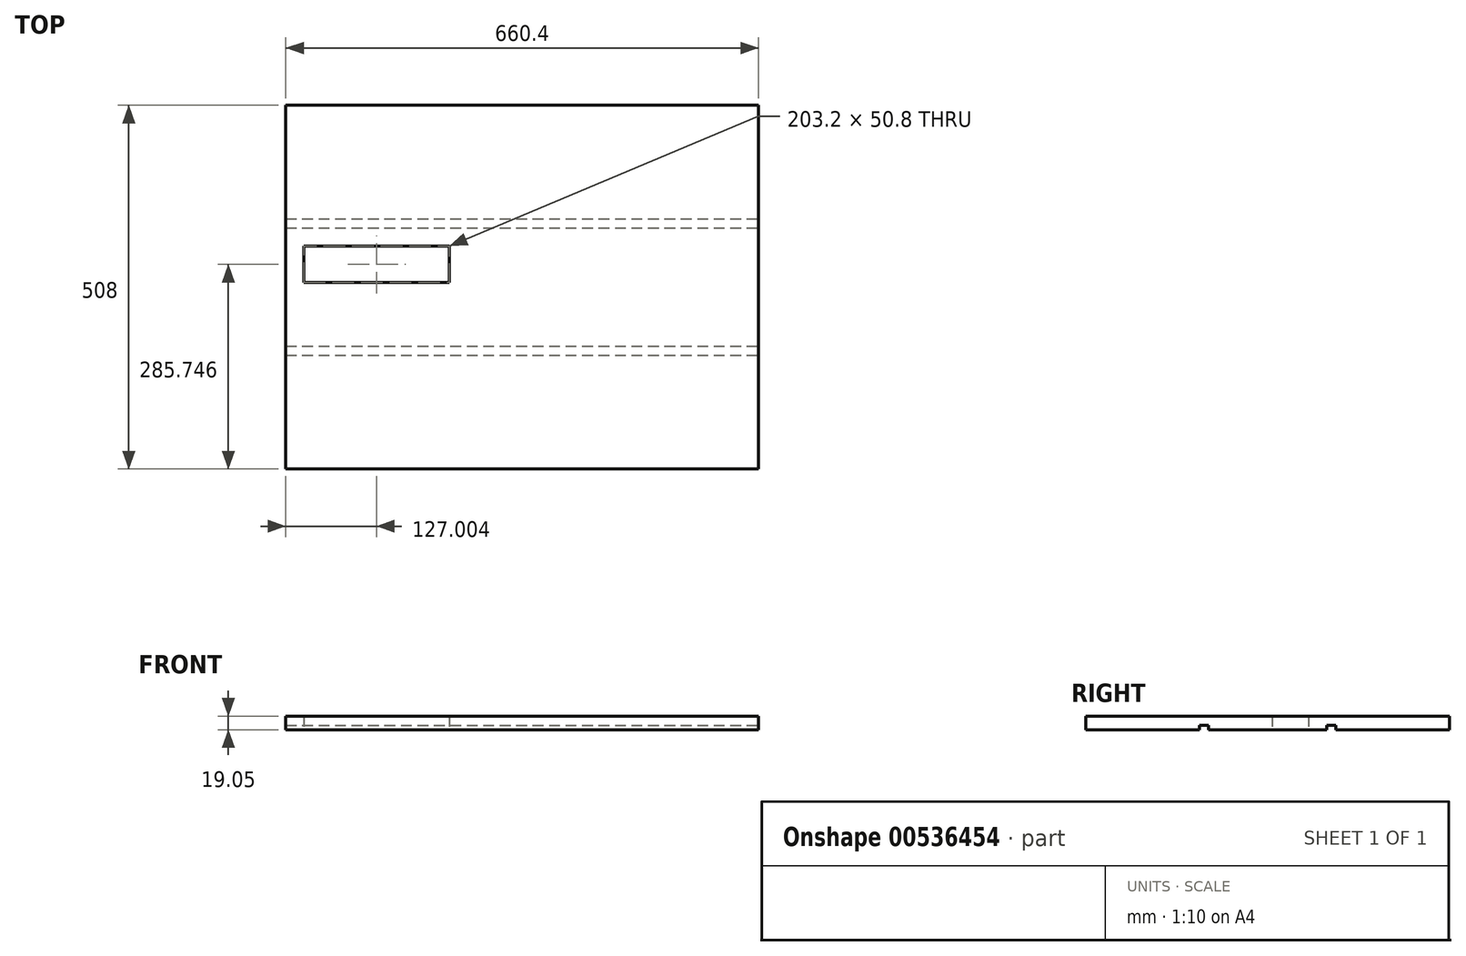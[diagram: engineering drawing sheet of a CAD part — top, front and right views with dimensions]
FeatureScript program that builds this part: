
annotation { "Feature Type Name" : "Feature", "Feature Type Description" : "" }
export const myFeature = defineFeature(function(context is Context, id is Id, definition is map)
    precondition{}
    {
        {
            var Q0;
            Q0=qCreatedBy(makeId("Top.planeOp"),FACE);
            var sketch = newSketch(context, id + "F0", { "sketchPlane" : qUnion([Q0])});
            skLineSegment(sketch, "E0.bottom", {"start": v(-46.34, 447.39) * mm, "end": v(614.06, 447.39) * mm});
            skLineSegment(sketch, "E0.top", {"start": v(-46.34, -60.61) * mm, "end": v(614.06, -60.61) * mm});
            skLineSegment(sketch, "E0.left", {"start": v(-46.34, 447.39) * mm, "end": v(-46.34, -60.61) * mm});
            skLineSegment(sketch, "E0.right", {"start": v(614.06, 447.39) * mm, "end": v(614.06, 415.64) * mm});
            skPoint(sketch, "E1.orphan", {"position": v(283.86, -60.61) * mm});
            skPoint(sketch, "E2.orphan", {"position": v(283.86, 447.39) * mm});
            skLineSegment(sketch, "E3.trimOffspring", {"start": v(614.06, 396.59) * mm, "end": v(614.06, -9.81) * mm});
            skLineSegment(sketch, "E4.trimOffspring", {"start": v(614.06, -28.86) * mm, "end": v(614.06, -60.61) * mm});
            skPoint(sketch, "E5.orphan", {"position": v(614.06, 193.39) * mm});
            skLineSegment(sketch, "E6", {"start": v(614.06, -9.81) * mm, "end": v(614.06, -28.86) * mm});
            skLineSegment(sketch, "E7", {"start": v(614.06, 396.59) * mm, "end": v(614.06, 415.64) * mm});
            skLineSegment(sketch, "E8", {"start": v(283.86, 447.39) * mm, "end": v(283.86, -60.61) * mm, "construction": true});
            skLineSegment(sketch, "E9.MirrorCS", {"start": v(182.26, 250.54) * mm, "end": v(182.26, 199.74) * mm});
            skLineSegment(sketch, "E10.MirrorCS", {"start": v(-20.94, 250.54) * mm, "end": v(182.26, 250.54) * mm});
            skLineSegment(sketch, "E11.MirrorCS", {"start": v(182.26, 199.74) * mm, "end": v(-20.94, 199.74) * mm});
            skLineSegment(sketch, "E12.MirrorCS", {"start": v(-20.94, 250.54) * mm, "end": v(-20.94, 199.74) * mm});
            skSolve(sketch);
        }
        {
            var Q0;
            Q0 = qSketchRegion(id + "F0", true);
            extrude(context, id + "F1", {"entities" : qUnion([Q0]), "depth" : 19.05 * mm, "offsetDistance" : 25.4 * mm});
        }
        {
            var Q0;
            Q0=makeQuery(id+"F1.opExtrude","CAP_FACE",FACE,{"disambiguationData":[OSD([sQuery(id+"F0.wireOp",EDGE,"E0.bottom"),sQuery(id+"F0.wireOp",EDGE,"E0.top"),sQuery(id+"F0.wireOp",EDGE,"E0.left"),sQuery(id+"F0.wireOp",EDGE,"E0.right"),sQuery(id+"F0.wireOp",EDGE,"E3.trimOffspring"),sQuery(id+"F0.wireOp",EDGE,"E4.trimOffspring"),sQuery(id+"F0.wireOp",EDGE,"i5BfIIhn-vbHe-imx1-csDb-nMQiqM2HRBRM.top"),sQuery(id+"F0.wireOp",EDGE,"i5BfIIhn-vbHe-imx1-csDb-nMQiqM2HRBRM.right"),sQuery(id+"F0.wireOp",EDGE,"78bbb6ff-89c4-4b25-9ef8-bd1ca9e1b5700.MirrorCS"),sQuery(id+"F0.wireOp",EDGE,"78bbb6ff-89c4-4b25-9ef8-bd1ca9e1b5701.MirrorCS"),sQuery(id+"F0.wireOp",EDGE,"ff8e6387-9dfd-4042-92c4-0e13fc46f2381.MirrorCS"),sQuery(id+"F0.wireOp",EDGE,"ff8e6387-9dfd-4042-92c4-0e13fc46f2382.MirrorCS"),sQuery(id+"F0.wireOp",EDGE,"lPivuiSJ-rouK-T9NZ-5f0i-5M2m3eOQRDiC"),sQuery(id+"F0.wireOp",EDGE,"E6"),sQuery(id+"F0.wireOp",EDGE,"E7")])],"isStart":true});
            var sketch = newSketch(context, id + "F2", { "sketchPlane" : qUnion([Q0])});
            skLineSegment(sketch, "E13.bottom", {"start": v(-46.34, 60.61) * mm, "end": v(614.06, 60.61) * mm});
            skLineSegment(sketch, "E13.top", {"start": v(-46.34, -447.39) * mm, "end": v(614.06, -447.39) * mm});
            skLineSegment(sketch, "E13.left", {"start": v(-46.34, -98.14) * mm, "end": v(-46.34, -110.84) * mm});
            skLineSegment(sketch, "E13.right", {"start": v(614.06, -98.14) * mm, "end": v(614.06, -110.84) * mm});
            skLineSegment(sketch, "E14.0", {"start": v(4.46, -282.29) * mm, "end": v(614.06, -282.29) * mm, "construction": true});
            skLineSegment(sketch, "E15.0", {"start": v(-46.34, -104.49) * mm, "end": v(563.26, -104.49) * mm, "construction": true});
            skLineSegment(sketch, "E16.0", {"start": v(-46.34, -110.84) * mm, "end": v(614.06, -110.84) * mm});
            skLineSegment(sketch, "E17.0", {"start": v(-46.34, -98.14) * mm, "end": v(614.06, -98.14) * mm});
            skLineSegment(sketch, "E18.0", {"start": v(-46.34, -288.64) * mm, "end": v(614.06, -288.64) * mm});
            skLineSegment(sketch, "E19.0", {"start": v(-46.34, -275.94) * mm, "end": v(614.06, -275.94) * mm});
            skLineSegment(sketch, "E20.trimOffspring", {"start": v(614.06, -275.94) * mm, "end": v(614.06, -288.64) * mm});
            skLineSegment(sketch, "E21.trimOffspring", {"start": v(-46.34, -275.94) * mm, "end": v(-46.34, -288.64) * mm});
            skSolve(sketch);
        }
        {
            var Q0;
            {var subQ1=sQuery(id+"F2.wireOp",EDGE,"ede1b310-70a5-4bce-ad08-636cf6eacef5.0");Q0=makeQuery(id+"F2.imprint","IMPRINT",FACE,{"disambiguationData":[TD([[makeQuery(id+"F2.imprint","IMPRINT",EDGE,{"derivedFrom":subQ1}),1.0]])]});}
            var Q1;
            {var subQ3=sQuery(id+"F2.wireOp",EDGE,"b575b931-e8e5-4f5f-8ae3-ec7b51b93ddb.0");Q1=makeQuery(id+"F2.imprint","IMPRINT",FACE,{"disambiguationData":[TD([[makeQuery(id+"F2.imprint","IMPRINT",EDGE,{"derivedFrom":subQ3}),-1.0]])]});}
            var Q2;
            Q2=makeQuery(id+"F2.imprint","IMPRINT",FACE,{"disambiguationData":[TD([[makeQuery(id+"F2.imprint","IMPRINT",EDGE,{"derivedFrom":sQuery(id+"F2.wireOp",EDGE,"E18.0")}),1.0]])]});
            var Q3;
            Q3=makeQuery(id+"F2.imprint","IMPRINT",FACE,{"disambiguationData":[TD([[makeQuery(id+"F2.imprint","IMPRINT",EDGE,{"derivedFrom":sQuery(id+"F2.wireOp",EDGE,"E13.left")}),-1.0]])]});
            extrude(context, id + "F3", {"entities" : qUnion([Q0, Q1, Q2, Q3]), "operationType" : NewBodyOperationType.REMOVE, "oppositeDirection" : true, "depth" : 6.35 * mm, "offsetDistance" : 25.4 * mm});
        }
    });
